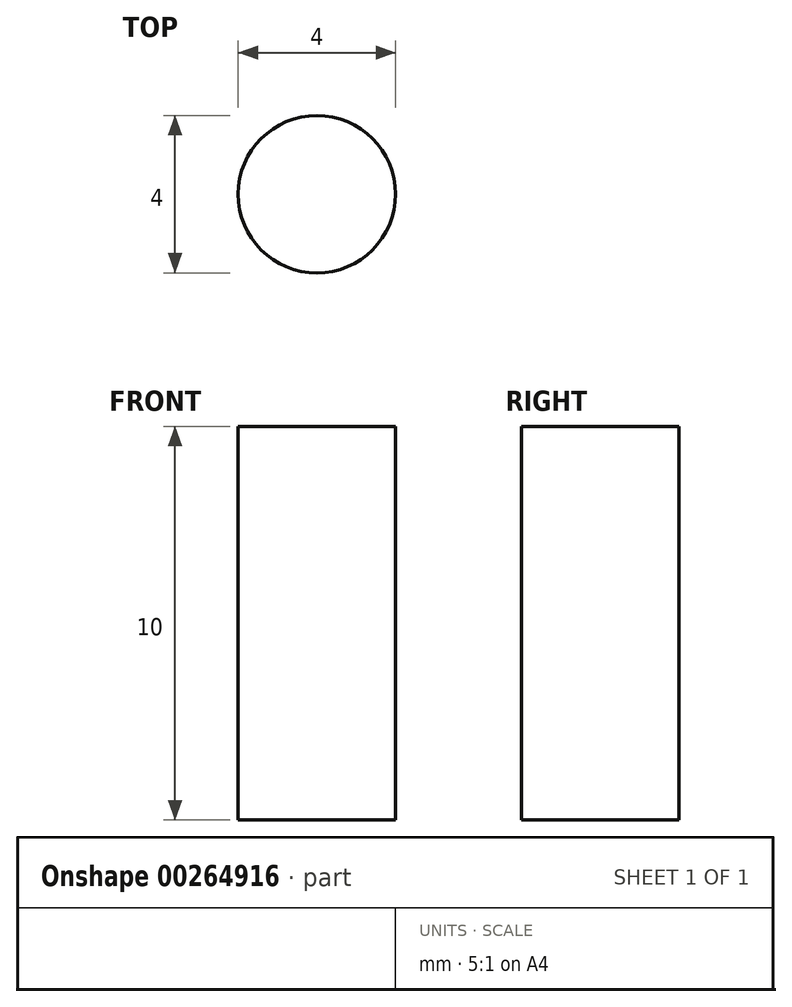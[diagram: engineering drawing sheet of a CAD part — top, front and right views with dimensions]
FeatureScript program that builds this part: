
annotation { "Feature Type Name" : "Feature", "Feature Type Description" : "" }
export const myFeature = defineFeature(function(context is Context, id is Id, definition is map)
    precondition{}
    {
        {
            var Q0;
            Q0=qCreatedBy(makeId("Top.planeOp"),FACE);
            var sketch = newSketch(context, id + "F0", { "sketchPlane" : qUnion([Q0])});
            skCircle(sketch, "E0", {"center": v(0, 0) * mm, "radius": 2 * mm});
            skSolve(sketch);
        }
        {
            var Q0;
            Q0 = qSketchRegion(id + "F0", true);
            extrude(context, id + "F1", {"entities" : qUnion([Q0]), "depth" : 10 * mm});
        }
    });
